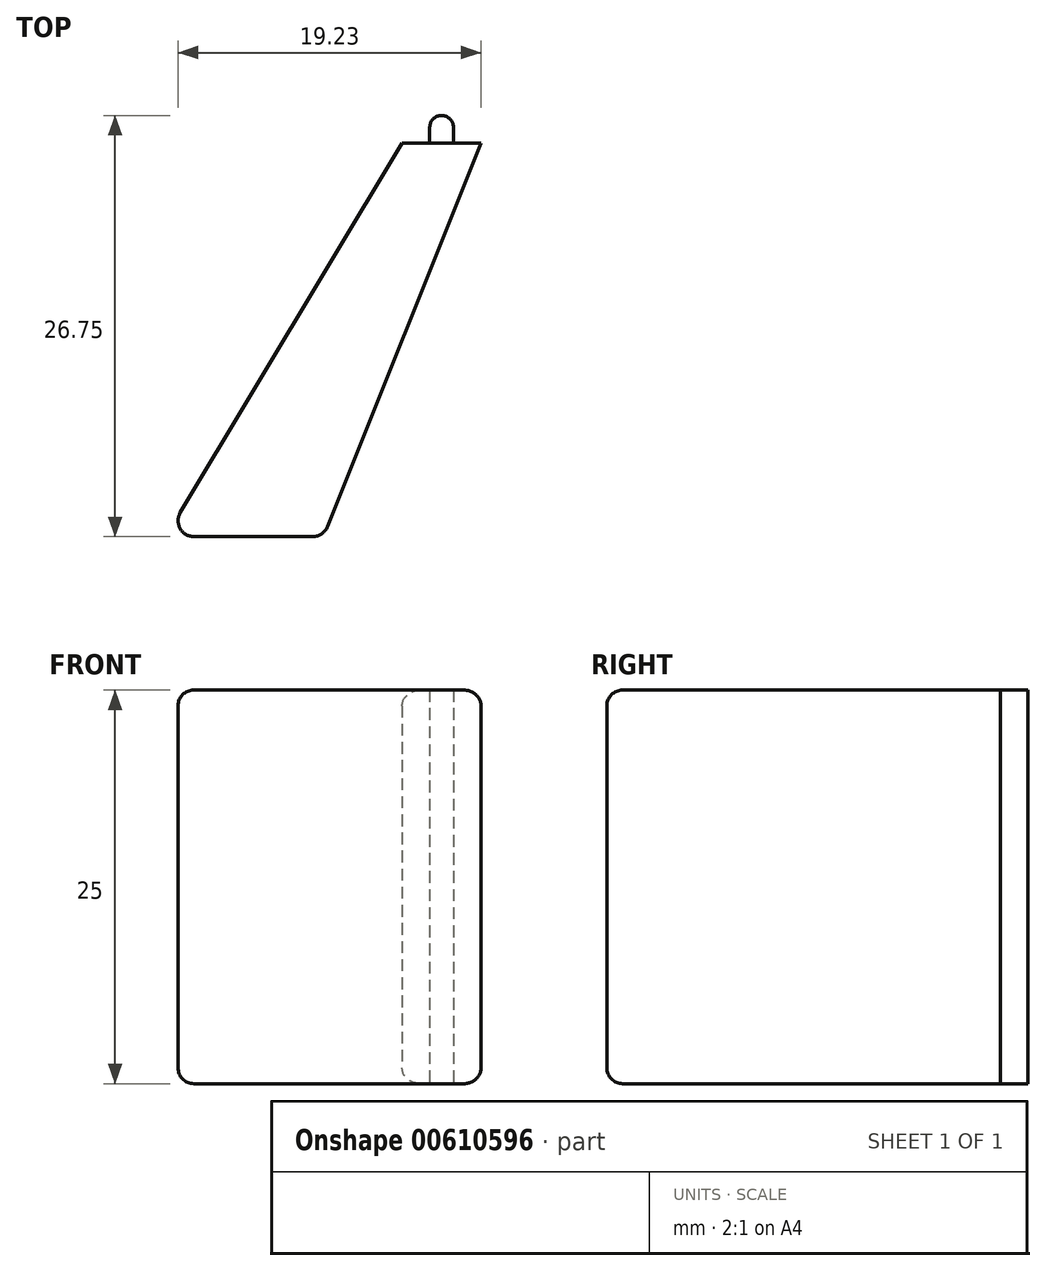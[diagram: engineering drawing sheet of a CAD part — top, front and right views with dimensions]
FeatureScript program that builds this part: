
annotation { "Feature Type Name" : "Feature", "Feature Type Description" : "" }
export const myFeature = defineFeature(function(context is Context, id is Id, definition is map)
    precondition{}
    {
        {
            var Q0;
            Q0=qCreatedBy(makeId("Top.planeOp"),FACE);
            var sketch = newSketch(context, id + "F0", { "sketchPlane" : qUnion([Q0])});
            skLineSegment(sketch, "E0", {"start": v(0, 0) * mm, "end": v(0, 20) * mm, "construction": true});
            skLineSegment(sketch, "E1", {"start": v(0, 10) * mm, "end": v(-22, 10) * mm});
            skLineSegment(sketch, "E2", {"start": v(-22, 10) * mm, "end": v(-22, 0) * mm});
            skLineSegment(sketch, "E3", {"start": v(-22, 0) * mm, "end": v(0, 0) * mm});
            skLineSegment(sketch, "E4", {"start": v(-22, 0) * mm, "end": v(-37, -25) * mm});
            skLineSegment(sketch, "E5", {"start": v(-37, -25) * mm, "end": v(-27, -25) * mm});
            skLineSegment(sketch, "E6", {"start": v(-27, -25) * mm, "end": v(-17, 0) * mm});
            skLineSegment(sketch, "E7", {"start": v(-22, 5) * mm, "end": v(-3.26, 5) * mm, "construction": true});
            skPoint(sketch, "E8", {"position": v(-17, 5) * mm});
            skLineSegment(sketch, "E9.MirrorCS", {"start": v(0, 10) * mm, "end": v(22, 10) * mm});
            skLineSegment(sketch, "E10.MirrorCS", {"start": v(22, 10) * mm, "end": v(22, 0) * mm});
            skPoint(sketch, "E11.MirrorP", {"position": v(17, 5) * mm});
            skLineSegment(sketch, "E12.MirrorCS", {"start": v(22, 0) * mm, "end": v(0, 0) * mm});
            skLineSegment(sketch, "E13.MirrorCS", {"start": v(27, -25) * mm, "end": v(17, 0) * mm});
            skLineSegment(sketch, "E14.MirrorCS", {"start": v(22, 0) * mm, "end": v(37, -25) * mm});
            skLineSegment(sketch, "E15.MirrorCS", {"start": v(37, -25) * mm, "end": v(27, -25) * mm});
            skSolve(sketch);
        }
        {
            var Q0;
            Q0=qCreatedBy(makeId("Top.planeOp"),FACE);
            var sketch = newSketch(context, id + "F1", { "sketchPlane" : qUnion([Q0])});
            skLineSegment(sketch, "E16.bottom", {"start": v(-20.25, 0) * mm, "end": v(-18.75, 0) * mm});
            skLineSegment(sketch, "E16.top", {"start": v(-20.25, 1) * mm, "end": v(-18.75, 1) * mm});
            skLineSegment(sketch, "E16.left", {"start": v(-20.25, 0) * mm, "end": v(-20.25, 1) * mm});
            skLineSegment(sketch, "E16.right", {"start": v(-18.75, 0) * mm, "end": v(-18.75, 1) * mm});
            skCircle(sketch, "E17", {"center": v(-19.5, 1) * mm, "radius": 0.75 * mm});
            skCircle(sketch, "E18.MirrorC", {"center": v(19.5, 1) * mm, "radius": 0.75 * mm});
            skLineSegment(sketch, "E19.MirrorCS", {"start": v(20.25, 0) * mm, "end": v(20.25, 1) * mm});
            skLineSegment(sketch, "E20.MirrorCS", {"start": v(18.75, 0) * mm, "end": v(18.75, 1) * mm});
            skLineSegment(sketch, "E21.MirrorCS", {"start": v(20.25, 0) * mm, "end": v(18.75, 0) * mm});
            skSolve(sketch);
        }
        {
            var Q0;
            {var subQ0=sQuery(id+"F0.wireOp",EDGE,"E4");Q0=makeQuery(id+"F0.imprint","IMPRINT",FACE,{"disambiguationData":[TD([[makeQuery(id+"F0.imprint","IMPRINT",EDGE,{"derivedFrom":subQ0}),1.0]])]});}
            var Q1;
            {var subQ2=sQuery(id+"F0.wireOp",EDGE,"E13.MirrorCS");Q1=makeQuery(id+"F0.imprint","IMPRINT",FACE,{"disambiguationData":[TD([[makeQuery(id+"F0.imprint","IMPRINT",EDGE,{"derivedFrom":subQ2}),-1.0]])]});}
            extrude(context, id + "F2", {"entities" : qUnion([Q0, Q1]), "depth" : 25 * mm, "offsetDistance" : 25 * mm});
        }
        {
            var Q0;
            Q0 = qSketchRegion(id + "F1", true);
            extrude(context, id + "F3", {"entities" : qUnion([Q0]), "depth" : 25 * mm, "offsetDistance" : 25 * mm});
        }
        {
            var Q0;
            Q0=makeQuery(id+"F3.opExtrude","SWEPT_BODY",BODY,{"disambiguationData":[OSD([sQuery(id+"F1.wireOp",EDGE,"E18.MirrorC"),sQuery(id+"F1.wireOp",EDGE,"E19.MirrorCS"),sQuery(id+"F1.wireOp",EDGE,"E20.MirrorCS"),sQuery(id+"F1.wireOp",EDGE,"E21.MirrorCS")])]});
            var Q1;
            Q1=makeQuery(id+"F2.opExtrude","SWEPT_BODY",BODY,{"disambiguationData":[OSD([sQuery(id+"F0.wireOp",EDGE,"E12.MirrorCS"),sQuery(id+"F0.wireOp",EDGE,"E13.MirrorCS"),sQuery(id+"F0.wireOp",EDGE,"E14.MirrorCS"),sQuery(id+"F0.wireOp",EDGE,"E15.MirrorCS")])]});
            deleteBodies(context, id + "F4", {"entities" : qUnion([Q0, Q1])});
        }
        {
            var Q0;
            Q0=makeQuery(id+"F2.opExtrude","CAP_EDGE",EDGE,{"disambiguationData":[OSD([sQuery(id+"F0.wireOp",EDGE,"E6")])],"isStart":true});
            var Q1;
            Q1=makeQuery(id+"F2.opExtrude","CAP_EDGE",EDGE,{"disambiguationData":[OSD([sQuery(id+"F0.wireOp",EDGE,"E4")])],"isStart":true});
            var Q2;
            Q2=makeQuery(id+"F2.opExtrude","CAP_EDGE",EDGE,{"disambiguationData":[OSD([sQuery(id+"F0.wireOp",EDGE,"E4")])],"isStart":false});
            var Q3;
            Q3=makeQuery(id+"F2.opExtrude","CAP_EDGE",EDGE,{"disambiguationData":[OSD([sQuery(id+"F0.wireOp",EDGE,"E6")])],"isStart":false});
            var Q4;
            Q4=makeQuery(id+"F2.opExtrude","CAP_EDGE",EDGE,{"disambiguationData":[OSD([sQuery(id+"F0.wireOp",EDGE,"E5")])],"isStart":true});
            var Q5;
            Q5=makeQuery(id+"F2.opExtrude","SWEPT_EDGE",EDGE,{"disambiguationData":[OSD([sQuery(id+"F0.wireOp",EDGE,"E5"),sQuery(id+"F0.wireOp",EDGE,"E6")])]});
            var Q6;
            Q6=makeQuery(id+"F2.opExtrude","SWEPT_EDGE",EDGE,{"disambiguationData":[OSD([sQuery(id+"F0.wireOp",EDGE,"E4"),sQuery(id+"F0.wireOp",EDGE,"E5")])]});
            var Q7;
            Q7=makeQuery(id+"F2.opExtrude","CAP_EDGE",EDGE,{"disambiguationData":[OSD([sQuery(id+"F0.wireOp",EDGE,"E5")])],"isStart":false});
            fillet(context, id + "F5", {"entities" : qUnion([Q0, Q1, Q2, Q3, Q4, Q5, Q6, Q7]), "radius" : 1 * mm, "tangentPropagation" : true, "allowEdgeOverflow" : false});
        }
    });
